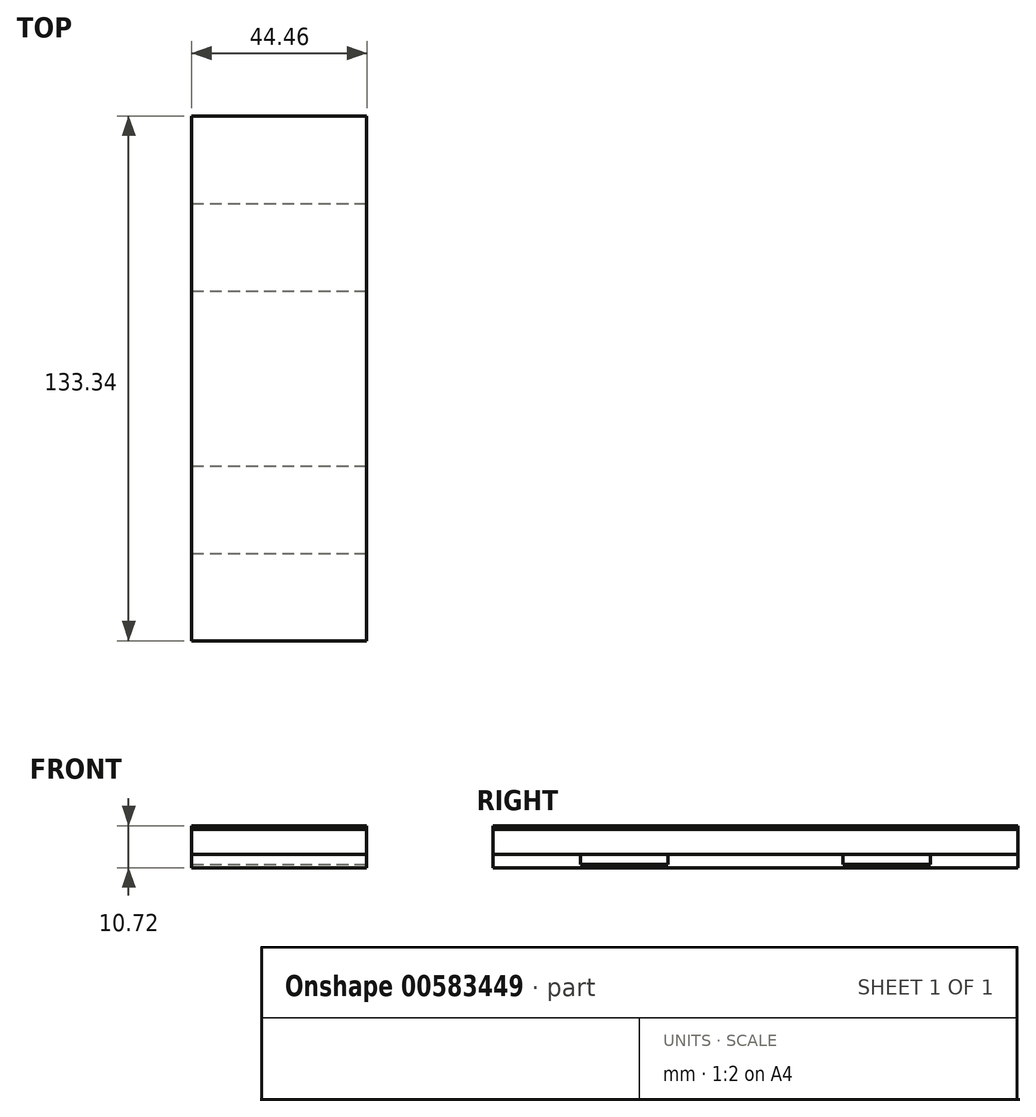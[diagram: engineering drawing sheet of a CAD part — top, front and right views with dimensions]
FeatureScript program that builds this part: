
annotation { "Feature Type Name" : "Feature", "Feature Type Description" : "" }
export const myFeature = defineFeature(function(context is Context, id is Id, definition is map)
    precondition{}
    {
        {
            assignVariable(context, id + "F0", {"name" : "Window", "anyValue" : 7 / 8});
        }
        {
            assignVariable(context, id + "F1", {"name" : "StackHeight", "anyValue" : 1.75});
        }
        {
            var Q0;
            Q0=qCreatedBy(makeId("Top.planeOp"),FACE);
            var sketch = newSketch(context, id + "F2", { "sketchPlane" : qUnion([Q0])});
            skLineSegment(sketch, "E0.bottom", {"start": v(-22.22, 66.68) * mm, "end": v(22.23, 66.68) * mm});
            skLineSegment(sketch, "E0.top", {"start": v(-22.22, -66.68) * mm, "end": v(22.23, -66.68) * mm});
            skLineSegment(sketch, "E0.left", {"start": v(-22.22, 66.68) * mm, "end": v(-22.22, -66.68) * mm});
            skLineSegment(sketch, "E0.right", {"start": v(22.23, 66.68) * mm, "end": v(22.23, -66.68) * mm});
            skPoint(sketch, "E0.middle", {"position": v(0, 0) * mm});
            skSolve(sketch);
        }
        {
            var Q0;
            Q0=makeQuery(id+"F2.imprint","IMPRINT",FACE,{"disambiguationData":[TD([[makeQuery(id+"F2.imprint","IMPRINT",EDGE,{"derivedFrom":sQuery(id+"F2.wireOp",EDGE,"E0.bottom")}),-1.0]])]});
            extrude(context, id + "F3", {"entities" : qUnion([Q0]), "depth" : (4 * getVariable(context, 'Window')) * mm});
        }
        {
            var Q0;
            Q0=makeQuery(id+"F3.opExtrude","CAP_FACE",FACE,{"disambiguationData":[OSD([sQuery(id+"F2.wireOp",EDGE,"E0.bottom"),sQuery(id+"F2.wireOp",EDGE,"E0.top"),sQuery(id+"F2.wireOp",EDGE,"E0.left"),sQuery(id+"F2.wireOp",EDGE,"E0.right")])],"isStart":false});
            var sketch = newSketch(context, id + "F4", { "sketchPlane" : qUnion([Q0])});
            skLineSegment(sketch, "E1", {"start": v(0, 0) * mm, "end": v(106.87, 0) * mm, "construction": true});
            skLineSegment(sketch, "E2", {"start": v(106.87, 0) * mm, "end": v(-89.53, 0) * mm, "construction": true});
            skLineSegment(sketch, "E3.bottom", {"start": v(-22.23, 22.22) * mm, "end": v(22.23, 22.22) * mm});
            skLineSegment(sketch, "E3.top", {"start": v(-22.23, 44.45) * mm, "end": v(22.23, 44.45) * mm});
            skLineSegment(sketch, "E3.left", {"start": v(-22.23, 22.22) * mm, "end": v(-22.23, 44.45) * mm});
            skLineSegment(sketch, "E3.right", {"start": v(22.23, 22.22) * mm, "end": v(22.23, 44.45) * mm});
            skLineSegment(sketch, "E4.MirrorCS", {"start": v(-22.23, -22.22) * mm, "end": v(22.23, -22.22) * mm});
            skLineSegment(sketch, "E5.MirrorCS", {"start": v(-22.23, -44.45) * mm, "end": v(22.23, -44.45) * mm});
            skLineSegment(sketch, "E6.MirrorCS", {"start": v(-22.23, -22.22) * mm, "end": v(-22.23, -44.45) * mm});
            skLineSegment(sketch, "E7.MirrorCS", {"start": v(22.23, -22.22) * mm, "end": v(22.23, -44.45) * mm});
            skSolve(sketch);
        }
        {
            var Q0;
            Q0=makeQuery(id+"F4.imprint","IMPRINT",FACE,{"disambiguationData":[TD([[makeQuery(id+"F4.imprint","IMPRINT",EDGE,{"derivedFrom":sQuery(id+"F4.wireOp",EDGE,"E4.MirrorCS")}),-1.0]])]});
            var Q1;
            Q1=makeQuery(id+"F4.imprint","IMPRINT",FACE,{"disambiguationData":[TD([[makeQuery(id+"F4.imprint","IMPRINT",EDGE,{"derivedFrom":sQuery(id+"F4.wireOp",EDGE,"E3.bottom")}),1.0]])]});
            extrude(context, id + "F5", {"entities" : qUnion([Q0, Q1]), "operationType" : NewBodyOperationType.REMOVE, "oppositeDirection" : true, "depth" : (3 * getVariable(context, 'Window')) * mm});
        }
        {
            var Q0;
            Q0=makeQuery(id+"F3.opExtrude","SWEPT_FACE",FACE,{"disambiguationData":[OSD([sQuery(id+"F2.wireOp",EDGE,"E0.left")])]});
            var sketch = newSketch(context, id + "F6", { "sketchPlane" : qUnion([Q0])});
            skLineSegment(sketch, "E8", {"start": v(-66.68, 11.11) * mm, "end": v(66.68, 11.11) * mm, "construction": true});
            skLineSegment(sketch, "E9", {"start": v(-55.56, 0) * mm, "end": v(-55.56, 88.9) * mm, "construction": true});
            skCircle(sketch, "E10", {"center": v(-55.56, 11.11) * mm, "radius": 3.57 * mm});
            skLineSegment(sketch, "E11", {"start": v(0, 0) * mm, "end": v(0, 88.9) * mm, "construction": true});
            skCircle(sketch, "E12.MirrorC", {"center": v(55.56, 11.11) * mm, "radius": 3.57 * mm});
            skSolve(sketch);
        }
        {
            var Q0;
            Q0=qSketchRegion(id+"F6",true);
            extrude(context, id + "F7", {"entities" : qUnion([Q0]), "operationType" : NewBodyOperationType.REMOVE, "oppositeDirection" : true, "depth" : (getVariable(context, 'StackHeight')) * mm});
        }
        {
            var Q0;
            {var subQ0=sQuery(id+"F2.wireOp",EDGE,"E0.bottom");var subQ1=sQuery(id+"F2.wireOp",EDGE,"E0.left");var subQ2=sQuery(id+"F2.wireOp",EDGE,"E0.right");Q0=makeQuery(id+"F5.boolean.opBoolean","SPLIT",FACE,{"disambiguationData":[TD([makeQuery(id+"F3.opExtrude","SWEPT_FACE",FACE,{"disambiguationData":[OSD([subQ0])]})])],"derivedFrom":makeQuery(id+"F3.opExtrude","CAP_FACE",FACE,{"disambiguationData":[OSD([subQ0,sQuery(id+"F2.wireOp",EDGE,"E0.top"),subQ1,subQ2])],"isStart":false})});}
            var sketch = newSketch(context, id + "F8", { "sketchPlane" : qUnion([Q0])});
            skPoint(sketch, "E13.oppositeSnap0", {"position": v(22.23, 55.56) * mm});
            skLineSegment(sketch, "E13.bottom", {"start": v(-22.23, 66.68) * mm, "end": v(22.23, 66.68) * mm});
            skLineSegment(sketch, "E13.top", {"start": v(-22.22, -66.68) * mm, "end": v(22.23, -66.68) * mm});
            skLineSegment(sketch, "E13.left", {"start": v(-22.23, 66.68) * mm, "end": v(-22.23, -66.68) * mm});
            skLineSegment(sketch, "E13.right", {"start": v(22.23, 66.68) * mm, "end": v(22.23, -66.68) * mm});
            skSolve(sketch);
        }
        {
            var Q0;
            Q0=qSketchRegion(id+"F8",true);
            extrude(context, id + "F9", {"entities" : qUnion([Q0]), "depth" : 6.35 * mm});
        }
        {
            var Q0;
            Q0=makeQuery(id+"F9.opExtrude","CAP_FACE",FACE,{"disambiguationData":[OSD([sQuery(id+"F8.wireOp",EDGE,"E13.bottom"),sQuery(id+"F8.wireOp",EDGE,"E13.top"),sQuery(id+"F8.wireOp",EDGE,"E13.left"),sQuery(id+"F8.wireOp",EDGE,"E13.right")])],"isStart":false});
            var sketch = newSketch(context, id + "F10", { "sketchPlane" : qUnion([Q0])});
            skLineSegment(sketch, "E14.bottom", {"start": v(-22.23, 66.68) * mm, "end": v(22.23, 66.68) * mm});
            skLineSegment(sketch, "E14.top", {"start": v(-22.23, -66.68) * mm, "end": v(22.23, -66.68) * mm});
            skLineSegment(sketch, "E14.left", {"start": v(-22.23, 66.68) * mm, "end": v(-22.23, -66.68) * mm});
            skLineSegment(sketch, "E14.right", {"start": v(22.23, 66.68) * mm, "end": v(22.23, -66.68) * mm});
            skSolve(sketch);
        }
        {
            var Q0;
            Q0=qSketchRegion(id+"F10",true);
            extrude(context, id + "F11", {"entities" : qUnion([Q0]), "depth" : (getVariable(context, 'Window')) * mm});
        }
        {
            var Q0;
            Q0=makeQuery(id+"F11.opExtrude","SWEPT_FACE",FACE,{"disambiguationData":[OSD([sQuery(id+"F10.wireOp",EDGE,"E14.left")])]});
            var sketch = newSketch(context, id + "F12", { "sketchPlane" : qUnion([Q0])});
            skLineSegment(sketch, "E15", {"start": v(-66.68, 106.36) * mm, "end": v(66.68, 106.36) * mm, "construction": true});
            skLineSegment(sketch, "E16", {"start": v(-55.56, 117.47) * mm, "end": v(-55.56, 0) * mm, "construction": true});
            skCircle(sketch, "E17", {"center": v(-55.56, 106.36) * mm, "radius": 3.57 * mm});
            skCircle(sketch, "E18.MirrorC", {"center": v(55.56, 106.36) * mm, "radius": 3.57 * mm});
            skSolve(sketch);
        }
        {
            var Q0;
            Q0=qSketchRegion(id+"F12",true);
            extrude(context, id + "F13", {"entities" : qUnion([Q0]), "operationType" : NewBodyOperationType.REMOVE, "oppositeDirection" : true, "depth" : (getVariable(context, 'StackHeight')) * mm});
        }
    });
